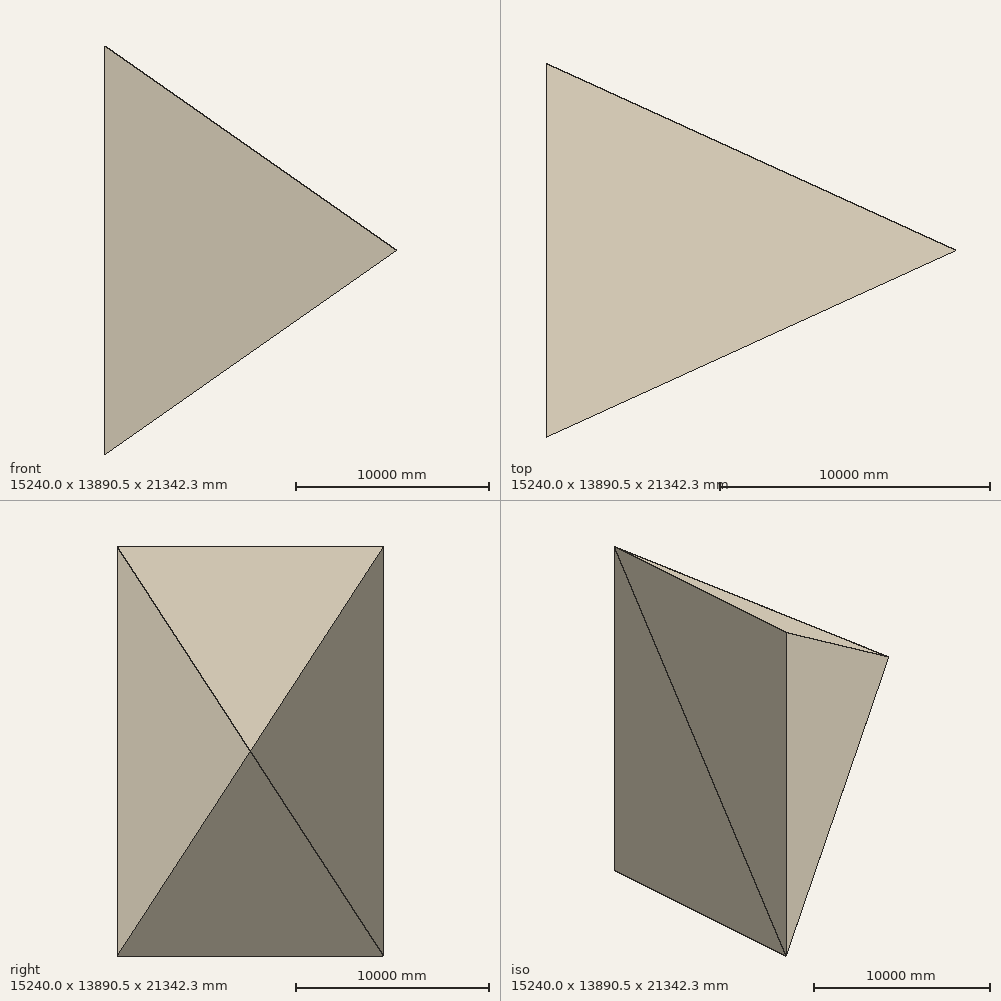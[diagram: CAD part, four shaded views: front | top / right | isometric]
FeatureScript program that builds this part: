
annotation { "Feature Type Name" : "Feature", "Feature Type Description" : "" }
export const myFeature = defineFeature(function(context is Context, id is Id, definition is map)
    precondition{}
    {
        {
            var Q0;
            Q0=qCreatedBy(makeId("Front.planeOp"),FACE);
            var sketch = newSketch(context, id + "F0", { "sketchPlane" : qUnion([Q0])});
            skLineSegment(sketch, "E0", {"start": v(0, 0) * mm, "end": v(-15240, 10671.16) * mm});
            skLineSegment(sketch, "E1", {"start": v(0, 0) * mm, "end": v(-15240, -10671.16) * mm});
            skLineSegment(sketch, "E2", {"start": v(-15240, -10671.16) * mm, "end": v(-15240, 10671.16) * mm});
            skSolve(sketch);
        }
        {
            var Q0;
            Q0=qCreatedBy(makeId("Top.planeOp"),FACE);
            var sketch = newSketch(context, id + "F1", { "sketchPlane" : qUnion([Q0])});
            skLineSegment(sketch, "E3", {"start": v(0, 0) * mm, "end": v(-15240, 6945.27) * mm});
            skLineSegment(sketch, "E4", {"start": v(-15240, 6945.27) * mm, "end": v(-15240, -6945.27) * mm});
            skLineSegment(sketch, "E5", {"start": v(-15240, -6945.27) * mm, "end": v(0, 0) * mm});
            skSolve(sketch);
        }
        {
            var Q0;
            Q0=makeQuery(id+"F0.imprint","IMPRINT",FACE,{"disambiguationData":[TD([[makeQuery(id+"F0.imprint","IMPRINT",EDGE,{"derivedFrom":sQuery(id+"F0.wireOp",EDGE,"E0")}),1.0]])]});
            var Q1;
            Q1=sQuery(id+"F1.wireOp",VERTEX,"E5.start");
            var Q2;
            Q2=sQuery(id+"F1.wireOp",VERTEX,"E4.start");
            extrude(context, id + "F2", {"entities" : qUnion([Q0]), "endBound" : BoundingType.UP_TO_VERTEX, "endBoundEntityVertex" : qUnion([Q1]), "depth" : 25.4 * mm, "hasSecondDirection" : true, "secondDirectionBound" : SecondDirectionBoundingType.UP_TO_VERTEX, "secondDirectionOppositeDirection" : true, "secondDirectionBoundEntityVertex" : qUnion([Q2]), "secondDirectionDepth" : 25.4 * mm});
        }
        {
            var Q0;
            Q0 = qSketchRegion(id + "F1", true);
            var Q1;
            Q1=sQuery(id+"F0.wireOp",VERTEX,"E2.end");
            var Q2;
            Q2=sQuery(id+"F0.wireOp",VERTEX,"E2.start");
            extrude(context, id + "F3", {"entities" : qUnion([Q0]), "operationType" : NewBodyOperationType.INTERSECT, "endBound" : BoundingType.UP_TO_VERTEX, "endBoundEntityVertex" : qUnion([Q1]), "depth" : 25.4 * mm, "hasSecondDirection" : true, "secondDirectionBound" : SecondDirectionBoundingType.UP_TO_VERTEX, "secondDirectionOppositeDirection" : true, "secondDirectionBoundEntityVertex" : qUnion([Q2]), "secondDirectionDepth" : 25.4 * mm});
        }
    });
